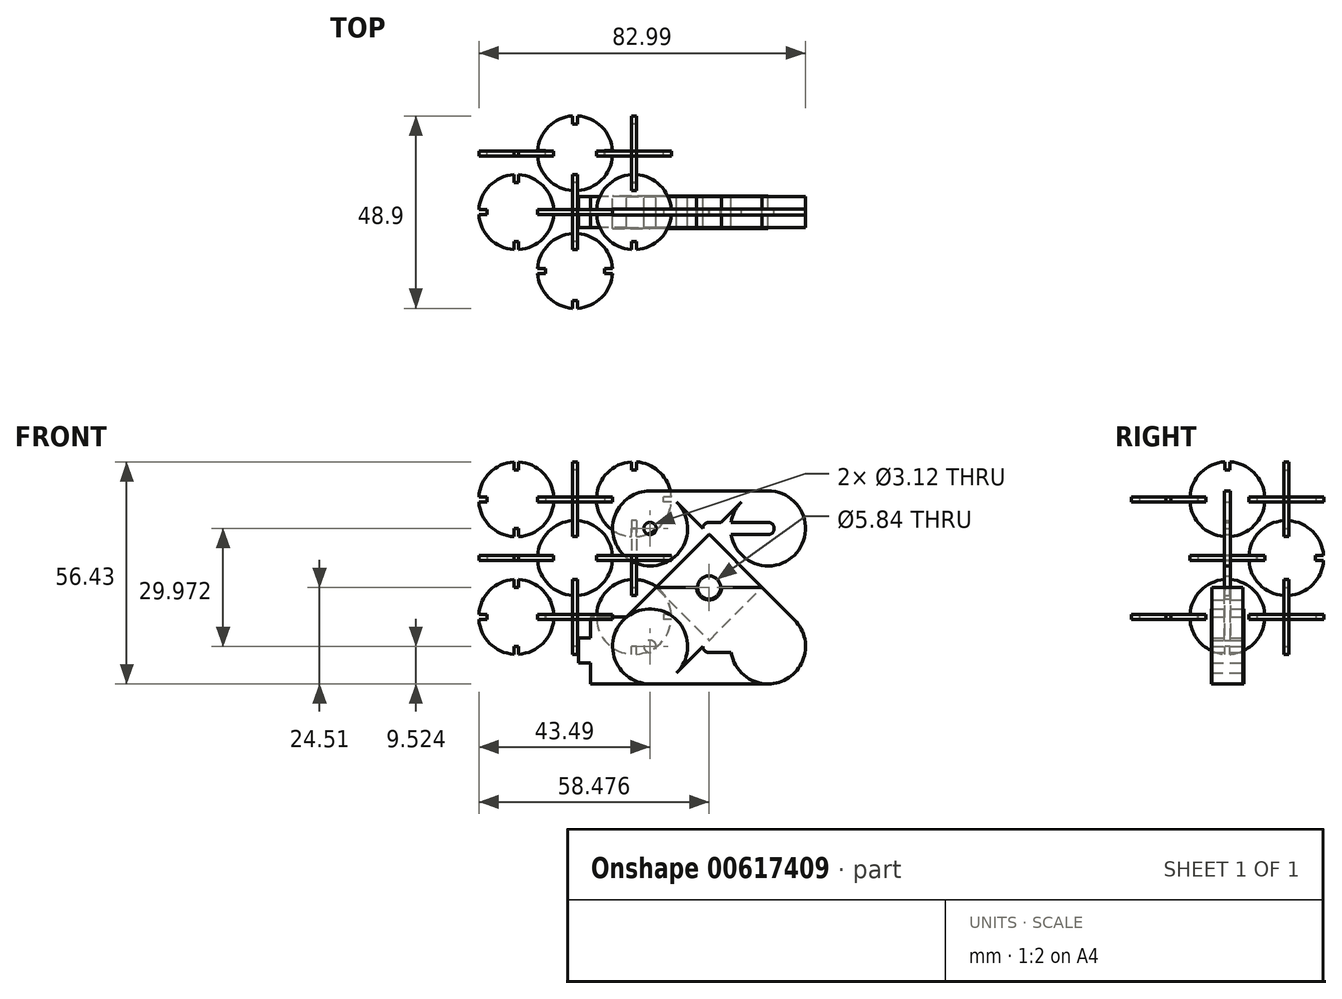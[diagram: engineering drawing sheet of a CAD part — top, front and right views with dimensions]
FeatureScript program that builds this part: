
annotation { "Feature Type Name" : "Feature", "Feature Type Description" : "" }
export const myFeature = defineFeature(function(context is Context, id is Id, definition is map)
    precondition{}
    {
        {
            var Q0;
            Q0=qCreatedBy(makeId("Front.planeOp"),FACE);
            var sketch = newSketch(context, id + "F0", { "sketchPlane" : qUnion([Q0])});
            skArc(sketch, "E0", {"start": v(-0.64, 16.98) * mm, "mid": v(-6.74, 14.2) * mm, "end": v(-9.5, 8.1) * mm});
            skLineSegment(sketch, "E1.top", {"start": v(-0.64, 14.94) * mm, "end": v(0.64, 14.94) * mm});
            skLineSegment(sketch, "E1.left", {"start": v(-0.64, 16.98) * mm, "end": v(-0.64, 14.94) * mm});
            skLineSegment(sketch, "E1.right", {"start": v(0.64, 16.98) * mm, "end": v(0.64, 14.94) * mm});
            skLineSegment(sketch, "E2.1.0", {"start": v(-9.5, 8.1) * mm, "end": v(-7.47, 8.1) * mm});
            skLineSegment(sketch, "E2.1.1", {"start": v(-7.47, 6.84) * mm, "end": v(-7.47, 8.1) * mm});
            skLineSegment(sketch, "E2.1.2", {"start": v(-9.5, 6.84) * mm, "end": v(-7.47, 6.84) * mm});
            skLineSegment(sketch, "E2.2.0", {"start": v(-0.64, -2.03) * mm, "end": v(-0.64, 0) * mm});
            skLineSegment(sketch, "E2.2.1", {"start": v(0.63, 0) * mm, "end": v(-0.64, 0) * mm});
            skLineSegment(sketch, "E2.2.2", {"start": v(0.63, -2.03) * mm, "end": v(0.63, 0) * mm});
            skLineSegment(sketch, "E2.3.0", {"start": v(9.5, 6.84) * mm, "end": v(7.47, 6.84) * mm});
            skLineSegment(sketch, "E2.3.1", {"start": v(7.47, 8.1) * mm, "end": v(7.47, 6.84) * mm});
            skLineSegment(sketch, "E2.3.2", {"start": v(9.5, 8.1) * mm, "end": v(7.47, 8.1) * mm});
            skArc(sketch, "E3.trimOffspring", {"start": v(9.5, 8.1) * mm, "mid": v(6.74, 14.2) * mm, "end": v(0.63, 16.98) * mm});
            skArc(sketch, "E4.trimOffspring", {"start": v(-9.5, 6.84) * mm, "mid": v(-6.74, 0.74) * mm, "end": v(-0.64, -2.03) * mm});
            skArc(sketch, "E5.trimOffspring", {"start": v(0.63, -2.03) * mm, "mid": v(6.74, 0.74) * mm, "end": v(9.5, 6.84) * mm});
            skSolve(sketch);
        }
        {
            var Q0;
            Q0=qCreatedBy(makeId("Right.planeOp"),FACE);
            var sketch = newSketch(context, id + "F1", { "sketchPlane" : qUnion([Q0])});
            skArc(sketch, "E6", {"start": v(-0.64, 2.03) * mm, "mid": v(-6.74, -0.74) * mm, "end": v(-9.5, -6.84) * mm});
            skLineSegment(sketch, "E7.top", {"start": v(-0.64, 0) * mm, "end": v(0.64, 0) * mm});
            skLineSegment(sketch, "E7.left", {"start": v(-0.64, 2.03) * mm, "end": v(-0.64, 0) * mm});
            skLineSegment(sketch, "E7.right", {"start": v(0.64, 2.03) * mm, "end": v(0.64, 0) * mm});
            skLineSegment(sketch, "E8.1.0", {"start": v(-9.5, -6.84) * mm, "end": v(-7.47, -6.84) * mm});
            skLineSegment(sketch, "E8.1.1", {"start": v(-7.47, -8.1) * mm, "end": v(-7.47, -6.84) * mm});
            skLineSegment(sketch, "E8.1.2", {"start": v(-9.5, -8.1) * mm, "end": v(-7.47, -8.1) * mm});
            skLineSegment(sketch, "E8.2.0", {"start": v(-0.64, -16.98) * mm, "end": v(-0.64, -14.94) * mm});
            skLineSegment(sketch, "E8.2.1", {"start": v(0.63, -14.94) * mm, "end": v(-0.64, -14.94) * mm});
            skLineSegment(sketch, "E8.2.2", {"start": v(0.63, -16.98) * mm, "end": v(0.63, -14.94) * mm});
            skLineSegment(sketch, "E8.3.0", {"start": v(9.5, -8.1) * mm, "end": v(7.47, -8.1) * mm});
            skLineSegment(sketch, "E8.3.1", {"start": v(7.47, -6.84) * mm, "end": v(7.47, -8.1) * mm});
            skLineSegment(sketch, "E8.3.2", {"start": v(9.5, -6.84) * mm, "end": v(7.47, -6.84) * mm});
            skArc(sketch, "E9.trimOffspring", {"start": v(9.5, -6.84) * mm, "mid": v(6.74, -0.74) * mm, "end": v(0.64, 2.03) * mm});
            skArc(sketch, "E10.trimOffspring", {"start": v(-9.5, -8.1) * mm, "mid": v(-6.74, -14.2) * mm, "end": v(-0.64, -16.98) * mm});
            skArc(sketch, "E11.trimOffspring", {"start": v(0.63, -16.98) * mm, "mid": v(6.74, -14.2) * mm, "end": v(9.5, -8.1) * mm});
            skArc(sketch, "E12", {"start": v(-0.64, 31.92) * mm, "mid": v(-6.74, 29.15) * mm, "end": v(-9.5, 23.05) * mm});
            skLineSegment(sketch, "E13.top", {"start": v(-0.64, 29.89) * mm, "end": v(0.64, 29.89) * mm});
            skLineSegment(sketch, "E13.left", {"start": v(-0.64, 31.92) * mm, "end": v(-0.64, 29.89) * mm});
            skLineSegment(sketch, "E13.right", {"start": v(0.64, 31.92) * mm, "end": v(0.64, 29.89) * mm});
            skLineSegment(sketch, "E14.1.0", {"start": v(-9.5, 23.05) * mm, "end": v(-7.47, 23.05) * mm});
            skLineSegment(sketch, "E14.1.1", {"start": v(-7.47, 21.78) * mm, "end": v(-7.47, 23.05) * mm});
            skLineSegment(sketch, "E14.1.2", {"start": v(-9.5, 21.78) * mm, "end": v(-7.47, 21.78) * mm});
            skLineSegment(sketch, "E14.2.0", {"start": v(-0.64, 12.91) * mm, "end": v(-0.64, 14.94) * mm});
            skLineSegment(sketch, "E14.2.1", {"start": v(0.63, 14.94) * mm, "end": v(-0.64, 14.94) * mm});
            skLineSegment(sketch, "E14.2.2", {"start": v(0.64, 12.91) * mm, "end": v(0.64, 14.94) * mm});
            skLineSegment(sketch, "E14.3.0", {"start": v(9.5, 21.78) * mm, "end": v(7.47, 21.78) * mm});
            skLineSegment(sketch, "E14.3.1", {"start": v(7.47, 23.05) * mm, "end": v(7.47, 21.78) * mm});
            skLineSegment(sketch, "E14.3.2", {"start": v(9.5, 23.05) * mm, "end": v(7.47, 23.05) * mm});
            skArc(sketch, "E15.trimOffspring", {"start": v(9.5, 23.05) * mm, "mid": v(6.74, 29.15) * mm, "end": v(0.63, 31.92) * mm});
            skArc(sketch, "E16.trimOffspring", {"start": v(-9.5, 21.78) * mm, "mid": v(-6.74, 15.68) * mm, "end": v(-0.64, 12.91) * mm});
            skArc(sketch, "E17.trimOffspring", {"start": v(0.64, 12.91) * mm, "mid": v(6.74, 15.68) * mm, "end": v(9.5, 21.78) * mm});
            skSolve(sketch);
        }
        {
            var Q0;
            Q0=qCreatedBy(makeId("Top.planeOp"),FACE);
            cPlane(context, id + "F2", {"entities" : qUnion([Q0]), "cplaneType" : CPlaneType.OFFSET, "offset" : 7.47 * mm, "width" : 152.4 * mm, "height" : 152.4 * mm});
        }
        {
            var Q0;
            Q0=qCreatedBy(makeId("Top.planeOp"),FACE);
            cPlane(context, id + "F3", {"entities" : qUnion([Q0]), "cplaneType" : CPlaneType.OFFSET, "offset" : 7.47 * mm, "oppositeDirection" : true, "width" : 152.4 * mm, "height" : 152.4 * mm});
        }
        {
            var Q0;
            Q0=qCreatedBy(id+"F2.planeOp",FACE);
            cPlane(context, id + "F4", {"entities" : qUnion([Q0]), "cplaneType" : CPlaneType.OFFSET, "offset" : 7.47 * mm, "width" : 152.4 * mm, "height" : 152.4 * mm});
        }
        {
            var Q0;
            Q0=qCreatedBy(id+"F4.planeOp",FACE);
            cPlane(context, id + "F5", {"entities" : qUnion([Q0]), "cplaneType" : CPlaneType.OFFSET, "offset" : 7.47 * mm, "width" : 152.4 * mm, "height" : 152.4 * mm});
        }
        {
            var Q0;
            Q0=qCreatedBy(makeId("Right.planeOp"),FACE);
            cPlane(context, id + "F6", {"entities" : qUnion([Q0]), "cplaneType" : CPlaneType.OFFSET, "offset" : 7.47 * mm, "width" : 152.4 * mm, "height" : 152.4 * mm});
        }
        {
            var Q0;
            Q0=qCreatedBy(id+"F6.planeOp",FACE);
            cPlane(context, id + "F7", {"entities" : qUnion([Q0]), "cplaneType" : CPlaneType.OFFSET, "offset" : 7.47 * mm, "width" : 152.4 * mm, "height" : 152.4 * mm});
        }
        {
            var Q0;
            Q0=qCreatedBy(makeId("Right.planeOp"),FACE);
            cPlane(context, id + "F8", {"entities" : qUnion([Q0]), "cplaneType" : CPlaneType.OFFSET, "offset" : 7.47 * mm, "oppositeDirection" : true, "width" : 152.4 * mm, "height" : 152.4 * mm});
        }
        {
            var Q0;
            Q0=qCreatedBy(id+"F8.planeOp",FACE);
            cPlane(context, id + "F9", {"entities" : qUnion([Q0]), "cplaneType" : CPlaneType.OFFSET, "offset" : 7.47 * mm, "oppositeDirection" : true, "width" : 152.4 * mm, "height" : 152.4 * mm});
        }
        {
            var Q0;
            Q0=qCreatedBy(makeId("Front.planeOp"),FACE);
            cPlane(context, id + "F10", {"entities" : qUnion([Q0]), "cplaneType" : CPlaneType.OFFSET, "offset" : 7.47 * mm, "width" : 152.4 * mm, "height" : 152.4 * mm});
        }
        {
            var Q0;
            Q0=qCreatedBy(id+"F10.planeOp",FACE);
            cPlane(context, id + "F11", {"entities" : qUnion([Q0]), "cplaneType" : CPlaneType.OFFSET, "offset" : 7.47 * mm, "width" : 152.4 * mm, "height" : 152.4 * mm});
        }
        {
            var Q0;
            Q0=qCreatedBy(makeId("Front.planeOp"),FACE);
            cPlane(context, id + "F12", {"entities" : qUnion([Q0]), "cplaneType" : CPlaneType.OFFSET, "offset" : 7.47 * mm, "oppositeDirection" : true, "width" : 152.4 * mm, "height" : 152.4 * mm});
        }
        {
            var Q0;
            Q0=qCreatedBy(id+"F12.planeOp",FACE);
            cPlane(context, id + "F13", {"entities" : qUnion([Q0]), "cplaneType" : CPlaneType.OFFSET, "offset" : 7.47 * mm, "oppositeDirection" : true, "width" : 152.4 * mm, "height" : 152.4 * mm});
        }
        {
            var Q0;
            Q0=qCreatedBy(id+"F2.planeOp",FACE);
            var sketch = newSketch(context, id + "F14", { "sketchPlane" : qUnion([Q0])});
            skArc(sketch, "E18", {"start": v(14.3, 9.5) * mm, "mid": v(8.2, 6.74) * mm, "end": v(5.43, 0.63) * mm});
            skLineSegment(sketch, "E19.top", {"start": v(14.3, 7.47) * mm, "end": v(15.57, 7.47) * mm});
            skLineSegment(sketch, "E19.left", {"start": v(14.3, 9.5) * mm, "end": v(14.3, 7.47) * mm});
            skLineSegment(sketch, "E19.right", {"start": v(15.57, 9.5) * mm, "end": v(15.57, 7.47) * mm});
            skLineSegment(sketch, "E20.1.0", {"start": v(5.43, 0.64) * mm, "end": v(7.46, 0.64) * mm});
            skLineSegment(sketch, "E20.1.1", {"start": v(7.46, -0.64) * mm, "end": v(7.46, 0.64) * mm});
            skLineSegment(sketch, "E20.1.2", {"start": v(5.43, -0.64) * mm, "end": v(7.46, -0.64) * mm});
            skLineSegment(sketch, "E20.2.0", {"start": v(14.3, -9.5) * mm, "end": v(14.3, -7.47) * mm});
            skLineSegment(sketch, "E20.2.1", {"start": v(15.57, -7.47) * mm, "end": v(14.3, -7.47) * mm});
            skLineSegment(sketch, "E20.2.2", {"start": v(15.57, -9.5) * mm, "end": v(15.57, -7.47) * mm});
            skLineSegment(sketch, "E20.3.0", {"start": v(24.44, -0.64) * mm, "end": v(22.4, -0.64) * mm});
            skLineSegment(sketch, "E20.3.1", {"start": v(22.4, 0.64) * mm, "end": v(22.4, -0.64) * mm});
            skLineSegment(sketch, "E20.3.2", {"start": v(24.44, 0.64) * mm, "end": v(22.4, 0.64) * mm});
            skArc(sketch, "E21.trimOffspring", {"start": v(24.44, 0.64) * mm, "mid": v(21.67, 6.74) * mm, "end": v(15.57, 9.5) * mm});
            skArc(sketch, "E22.trimOffspring", {"start": v(5.43, -0.63) * mm, "mid": v(8.2, -6.74) * mm, "end": v(14.3, -9.5) * mm});
            skArc(sketch, "E23.trimOffspring", {"start": v(15.57, -9.5) * mm, "mid": v(21.67, -6.74) * mm, "end": v(24.44, -0.63) * mm});
            skArc(sketch, "E24", {"start": v(-15.57, 9.5) * mm, "mid": v(-21.67, 6.74) * mm, "end": v(-24.44, 0.63) * mm});
            skLineSegment(sketch, "E25.top", {"start": v(-15.57, 7.47) * mm, "end": v(-14.3, 7.47) * mm});
            skLineSegment(sketch, "E25.left", {"start": v(-15.57, 9.5) * mm, "end": v(-15.57, 7.47) * mm});
            skLineSegment(sketch, "E25.right", {"start": v(-14.3, 9.5) * mm, "end": v(-14.3, 7.47) * mm});
            skLineSegment(sketch, "E26.1.0", {"start": v(-24.44, 0.63) * mm, "end": v(-22.4, 0.63) * mm});
            skLineSegment(sketch, "E26.1.1", {"start": v(-22.4, -0.64) * mm, "end": v(-22.4, 0.64) * mm});
            skLineSegment(sketch, "E26.1.2", {"start": v(-24.44, -0.64) * mm, "end": v(-22.4, -0.64) * mm});
            skLineSegment(sketch, "E26.2.0", {"start": v(-15.57, -9.5) * mm, "end": v(-15.57, -7.47) * mm});
            skLineSegment(sketch, "E26.2.1", {"start": v(-14.3, -7.47) * mm, "end": v(-15.57, -7.47) * mm});
            skLineSegment(sketch, "E26.2.2", {"start": v(-14.3, -9.5) * mm, "end": v(-14.3, -7.47) * mm});
            skLineSegment(sketch, "E26.3.0", {"start": v(-5.43, -0.64) * mm, "end": v(-7.46, -0.64) * mm});
            skLineSegment(sketch, "E26.3.1", {"start": v(-7.46, 0.64) * mm, "end": v(-7.46, -0.64) * mm});
            skLineSegment(sketch, "E26.3.2", {"start": v(-5.43, 0.64) * mm, "end": v(-7.46, 0.64) * mm});
            skArc(sketch, "E27.trimOffspring", {"start": v(-5.43, 0.63) * mm, "mid": v(-8.2, 6.74) * mm, "end": v(-14.3, 9.5) * mm});
            skArc(sketch, "E28.trimOffspring", {"start": v(-24.44, -0.63) * mm, "mid": v(-21.67, -6.74) * mm, "end": v(-15.57, -9.5) * mm});
            skArc(sketch, "E29.trimOffspring", {"start": v(-14.3, -9.5) * mm, "mid": v(-8.2, -6.74) * mm, "end": v(-5.43, -0.63) * mm});
            skSolve(sketch);
        }
        {
            var Q0;
            Q0=qCreatedBy(id+"F13.planeOp",FACE);
            var sketch = newSketch(context, id + "F15", { "sketchPlane" : qUnion([Q0])});
            skArc(sketch, "E30", {"start": v(-15.57, 31.91) * mm, "mid": v(-21.67, 29.14) * mm, "end": v(-24.44, 23.04) * mm});
            skLineSegment(sketch, "E31.top", {"start": v(-15.57, 29.88) * mm, "end": v(-14.3, 29.88) * mm});
            skLineSegment(sketch, "E31.left", {"start": v(-15.57, 31.91) * mm, "end": v(-15.57, 29.88) * mm});
            skLineSegment(sketch, "E31.right", {"start": v(-14.3, 31.91) * mm, "end": v(-14.3, 29.88) * mm});
            skLineSegment(sketch, "E32.1.0", {"start": v(-24.44, 23.04) * mm, "end": v(-22.4, 23.04) * mm});
            skLineSegment(sketch, "E32.1.1", {"start": v(-22.4, 21.77) * mm, "end": v(-22.4, 23.04) * mm});
            skLineSegment(sketch, "E32.1.2", {"start": v(-24.44, 21.77) * mm, "end": v(-22.4, 21.77) * mm});
            skLineSegment(sketch, "E32.2.0", {"start": v(-15.57, 12.9) * mm, "end": v(-15.57, 14.94) * mm});
            skLineSegment(sketch, "E32.2.1", {"start": v(-14.3, 14.94) * mm, "end": v(-15.57, 14.94) * mm});
            skLineSegment(sketch, "E32.2.2", {"start": v(-14.3, 12.9) * mm, "end": v(-14.3, 14.94) * mm});
            skLineSegment(sketch, "E32.3.0", {"start": v(-5.43, 21.77) * mm, "end": v(-7.46, 21.77) * mm});
            skLineSegment(sketch, "E32.3.1", {"start": v(-7.46, 23.04) * mm, "end": v(-7.46, 21.77) * mm});
            skLineSegment(sketch, "E32.3.2", {"start": v(-5.43, 23.04) * mm, "end": v(-7.46, 23.04) * mm});
            skArc(sketch, "E33.trimOffspring", {"start": v(-5.43, 23.04) * mm, "mid": v(-8.2, 29.14) * mm, "end": v(-14.3, 31.91) * mm});
            skArc(sketch, "E34.trimOffspring", {"start": v(-24.44, 21.77) * mm, "mid": v(-21.67, 15.67) * mm, "end": v(-15.57, 12.9) * mm});
            skArc(sketch, "E35.trimOffspring", {"start": v(-14.3, 12.9) * mm, "mid": v(-8.2, 15.67) * mm, "end": v(-5.43, 21.77) * mm});
            skLineSegment(sketch, "E36.MirrorCS", {"start": v(-15.57, -16.98) * mm, "end": v(-15.57, -14.94) * mm});
            skLineSegment(sketch, "E37.MirrorCS", {"start": v(-14.3, -16.98) * mm, "end": v(-14.3, -14.94) * mm});
            skLineSegment(sketch, "E38.MirrorCS", {"start": v(-15.57, 2.03) * mm, "end": v(-15.57, 0) * mm});
            skLineSegment(sketch, "E39.MirrorCS", {"start": v(-24.44, -6.84) * mm, "end": v(-22.4, -6.84) * mm});
            skLineSegment(sketch, "E40.MirrorCS", {"start": v(-5.43, -8.1) * mm, "end": v(-7.46, -8.1) * mm});
            skLineSegment(sketch, "E41.MirrorCS", {"start": v(-24.44, -8.1) * mm, "end": v(-22.4, -8.1) * mm});
            skLineSegment(sketch, "E42.MirrorCS", {"start": v(-22.4, -6.84) * mm, "end": v(-22.4, -8.1) * mm});
            skLineSegment(sketch, "E43.MirrorCS", {"start": v(-14.3, 0) * mm, "end": v(-15.57, 0) * mm});
            skLineSegment(sketch, "E44.MirrorCS", {"start": v(-5.43, -6.84) * mm, "end": v(-7.46, -6.84) * mm});
            skLineSegment(sketch, "E45.MirrorCS", {"start": v(-15.57, -14.94) * mm, "end": v(-14.3, -14.94) * mm});
            skLineSegment(sketch, "E46.MirrorCS", {"start": v(-14.3, 2.03) * mm, "end": v(-14.3, 0) * mm});
            skLineSegment(sketch, "E47.MirrorCS", {"start": v(-7.46, -8.1) * mm, "end": v(-7.46, -6.84) * mm});
            skArc(sketch, "E48.MirrorCS", {"start": v(-5.43, -8.1) * mm, "mid": v(-8.2, -14.2) * mm, "end": v(-14.3, -16.98) * mm});
            skArc(sketch, "E49.MirrorCS", {"start": v(-14.3, 2.03) * mm, "mid": v(-8.2, -0.74) * mm, "end": v(-5.43, -6.84) * mm});
            skArc(sketch, "E50.MirrorCS", {"start": v(-24.44, -6.84) * mm, "mid": v(-21.67, -0.74) * mm, "end": v(-15.57, 2.03) * mm});
            skArc(sketch, "E51.MirrorCS", {"start": v(-15.57, -16.98) * mm, "mid": v(-21.67, -14.2) * mm, "end": v(-24.44, -8.1) * mm});
            skLineSegment(sketch, "E52.MirrorCS", {"start": v(7.46, -8.1) * mm, "end": v(7.46, -6.84) * mm});
            skLineSegment(sketch, "E53.MirrorCS", {"start": v(15.57, -16.98) * mm, "end": v(15.57, -14.94) * mm});
            skLineSegment(sketch, "E54.MirrorCS", {"start": v(5.43, 23.04) * mm, "end": v(7.46, 23.04) * mm});
            skLineSegment(sketch, "E55.MirrorCS", {"start": v(24.44, -8.1) * mm, "end": v(22.4, -8.1) * mm});
            skLineSegment(sketch, "E56.MirrorCS", {"start": v(24.44, 23.04) * mm, "end": v(22.4, 23.04) * mm});
            skLineSegment(sketch, "E57.MirrorCS", {"start": v(22.4, 21.77) * mm, "end": v(22.4, 23.04) * mm});
            skLineSegment(sketch, "E58.MirrorCS", {"start": v(24.44, -6.84) * mm, "end": v(22.4, -6.84) * mm});
            skLineSegment(sketch, "E59.MirrorCS", {"start": v(14.3, 12.9) * mm, "end": v(14.3, 14.94) * mm});
            skLineSegment(sketch, "E60.MirrorCS", {"start": v(15.57, 31.91) * mm, "end": v(15.57, 29.88) * mm});
            skLineSegment(sketch, "E61.MirrorCS", {"start": v(5.43, -6.84) * mm, "end": v(7.46, -6.84) * mm});
            skLineSegment(sketch, "E62.MirrorCS", {"start": v(5.43, 21.77) * mm, "end": v(7.46, 21.77) * mm});
            skLineSegment(sketch, "E63.MirrorCS", {"start": v(7.46, 23.04) * mm, "end": v(7.46, 21.77) * mm});
            skLineSegment(sketch, "E64.MirrorCS", {"start": v(14.3, 2.03) * mm, "end": v(14.3, 0) * mm});
            skLineSegment(sketch, "E65.MirrorCS", {"start": v(15.57, 2.03) * mm, "end": v(15.57, 0) * mm});
            skLineSegment(sketch, "E66.MirrorCS", {"start": v(5.43, -8.1) * mm, "end": v(7.46, -8.1) * mm});
            skLineSegment(sketch, "E67.MirrorCS", {"start": v(14.3, -16.98) * mm, "end": v(14.3, -14.94) * mm});
            skLineSegment(sketch, "E68.MirrorCS", {"start": v(24.44, 21.77) * mm, "end": v(22.4, 21.77) * mm});
            skLineSegment(sketch, "E69.MirrorCS", {"start": v(15.57, -14.94) * mm, "end": v(14.3, -14.94) * mm});
            skLineSegment(sketch, "E70.MirrorCS", {"start": v(22.4, -6.84) * mm, "end": v(22.4, -8.1) * mm});
            skLineSegment(sketch, "E71.MirrorCS", {"start": v(14.3, 0) * mm, "end": v(15.57, 0) * mm});
            skLineSegment(sketch, "E72.MirrorCS", {"start": v(14.3, 31.91) * mm, "end": v(14.3, 29.88) * mm});
            skLineSegment(sketch, "E73.MirrorCS", {"start": v(14.3, 14.94) * mm, "end": v(15.57, 14.94) * mm});
            skLineSegment(sketch, "E74.MirrorCS", {"start": v(15.57, 29.88) * mm, "end": v(14.3, 29.88) * mm});
            skLineSegment(sketch, "E75.MirrorCS", {"start": v(15.57, 12.9) * mm, "end": v(15.57, 14.94) * mm});
            skArc(sketch, "E76.MirrorCS", {"start": v(14.3, 12.9) * mm, "mid": v(8.2, 15.67) * mm, "end": v(5.43, 21.77) * mm});
            skArc(sketch, "E77.MirrorCS", {"start": v(14.3, 2.03) * mm, "mid": v(8.2, -0.74) * mm, "end": v(5.43, -6.84) * mm});
            skArc(sketch, "E78.MirrorCS", {"start": v(5.43, -8.1) * mm, "mid": v(8.2, -14.2) * mm, "end": v(14.3, -16.98) * mm});
            skArc(sketch, "E79.MirrorCS", {"start": v(24.44, 21.77) * mm, "mid": v(21.67, 15.67) * mm, "end": v(15.57, 12.9) * mm});
            skArc(sketch, "E80.MirrorCS", {"start": v(15.57, -16.98) * mm, "mid": v(21.67, -14.2) * mm, "end": v(24.44, -8.1) * mm});
            skArc(sketch, "E81.MirrorCS", {"start": v(5.43, 23.04) * mm, "mid": v(8.2, 29.14) * mm, "end": v(14.3, 31.91) * mm});
            skArc(sketch, "E82.MirrorCS", {"start": v(24.44, -6.84) * mm, "mid": v(21.67, -0.74) * mm, "end": v(15.57, 2.03) * mm});
            skArc(sketch, "E83.MirrorCS", {"start": v(15.57, 31.91) * mm, "mid": v(21.67, 29.14) * mm, "end": v(24.44, 23.04) * mm});
            skSolve(sketch);
        }
        {
            var Q0;
            Q0=qCreatedBy(id+"F11.planeOp",FACE);
            var sketch = newSketch(context, id + "F16", { "sketchPlane" : qUnion([Q0])});
            skArc(sketch, "E84", {"start": v(14.3, 2.03) * mm, "mid": v(8.2, -0.73) * mm, "end": v(5.43, -6.83) * mm});
            skLineSegment(sketch, "E85.top", {"start": v(14.3, 0) * mm, "end": v(15.57, 0) * mm});
            skLineSegment(sketch, "E85.left", {"start": v(14.3, 2.03) * mm, "end": v(14.3, 0) * mm});
            skLineSegment(sketch, "E85.right", {"start": v(15.57, 2.03) * mm, "end": v(15.57, 0) * mm});
            skLineSegment(sketch, "E86.1.0", {"start": v(5.43, -6.83) * mm, "end": v(7.46, -6.83) * mm});
            skLineSegment(sketch, "E86.1.1", {"start": v(7.46, -8.1) * mm, "end": v(7.46, -6.83) * mm});
            skLineSegment(sketch, "E86.1.2", {"start": v(5.43, -8.1) * mm, "end": v(7.46, -8.1) * mm});
            skLineSegment(sketch, "E86.2.0", {"start": v(14.3, -16.98) * mm, "end": v(14.3, -14.94) * mm});
            skLineSegment(sketch, "E86.2.1", {"start": v(15.57, -14.94) * mm, "end": v(14.3, -14.94) * mm});
            skLineSegment(sketch, "E86.2.2", {"start": v(15.57, -16.98) * mm, "end": v(15.57, -14.94) * mm});
            skLineSegment(sketch, "E86.3.0", {"start": v(24.44, -8.11) * mm, "end": v(22.4, -8.11) * mm});
            skLineSegment(sketch, "E86.3.1", {"start": v(22.4, -6.84) * mm, "end": v(22.4, -8.11) * mm});
            skLineSegment(sketch, "E86.3.2", {"start": v(24.44, -6.84) * mm, "end": v(22.4, -6.84) * mm});
            skArc(sketch, "E87.trimOffspring", {"start": v(24.44, -6.84) * mm, "mid": v(21.67, -0.74) * mm, "end": v(15.57, 2.03) * mm});
            skArc(sketch, "E88.trimOffspring", {"start": v(5.43, -8.1) * mm, "mid": v(8.2, -14.2) * mm, "end": v(14.3, -16.98) * mm});
            skArc(sketch, "E89.trimOffspring", {"start": v(15.57, -16.98) * mm, "mid": v(21.67, -14.21) * mm, "end": v(24.44, -8.11) * mm});
            skLineSegment(sketch, "E90.MirrorCS", {"start": v(22.4, 21.78) * mm, "end": v(22.4, 23.05) * mm});
            skLineSegment(sketch, "E91.MirrorCS", {"start": v(15.57, 29.88) * mm, "end": v(14.3, 29.88) * mm});
            skLineSegment(sketch, "E92.MirrorCS", {"start": v(7.46, 23.04) * mm, "end": v(7.46, 21.77) * mm});
            skLineSegment(sketch, "E93.MirrorCS", {"start": v(14.3, 14.93) * mm, "end": v(15.57, 14.93) * mm});
            skLineSegment(sketch, "E94.MirrorCS", {"start": v(24.44, 21.78) * mm, "end": v(22.4, 21.78) * mm});
            skLineSegment(sketch, "E95.MirrorCS", {"start": v(15.57, 31.91) * mm, "end": v(15.57, 29.88) * mm});
            skLineSegment(sketch, "E96.MirrorCS", {"start": v(24.44, 23.05) * mm, "end": v(22.4, 23.05) * mm});
            skLineSegment(sketch, "E97.MirrorCS", {"start": v(14.3, 31.91) * mm, "end": v(14.3, 29.88) * mm});
            skArc(sketch, "E98.MirrorCS", {"start": v(5.43, 23.04) * mm, "mid": v(8.2, 29.14) * mm, "end": v(14.3, 31.91) * mm});
            skArc(sketch, "E99.MirrorCS", {"start": v(14.3, 12.9) * mm, "mid": v(8.2, 15.67) * mm, "end": v(5.43, 21.77) * mm});
            skLineSegment(sketch, "E100.MirrorCS", {"start": v(5.43, 21.77) * mm, "end": v(7.46, 21.77) * mm});
            skLineSegment(sketch, "E101.MirrorCS", {"start": v(15.57, 12.9) * mm, "end": v(15.57, 14.93) * mm});
            skArc(sketch, "E102.MirrorCS", {"start": v(15.57, 31.91) * mm, "mid": v(21.67, 29.15) * mm, "end": v(24.44, 23.05) * mm});
            skLineSegment(sketch, "E103.MirrorCS", {"start": v(5.43, 23.04) * mm, "end": v(7.46, 23.04) * mm});
            skLineSegment(sketch, "E104.MirrorCS", {"start": v(14.3, 12.9) * mm, "end": v(14.3, 14.93) * mm});
            skArc(sketch, "E105.MirrorCS", {"start": v(24.44, 21.78) * mm, "mid": v(21.67, 15.68) * mm, "end": v(15.57, 12.9) * mm});
            skLineSegment(sketch, "E106.MirrorCS", {"start": v(-7.46, -8.1) * mm, "end": v(-7.46, -6.83) * mm});
            skLineSegment(sketch, "E107.MirrorCS", {"start": v(-14.3, 14.93) * mm, "end": v(-15.57, 14.93) * mm});
            skLineSegment(sketch, "E108.MirrorCS", {"start": v(-15.57, 29.88) * mm, "end": v(-14.3, 29.88) * mm});
            skLineSegment(sketch, "E109.MirrorCS", {"start": v(-14.3, 0) * mm, "end": v(-15.57, 0) * mm});
            skLineSegment(sketch, "E110.MirrorCS", {"start": v(-7.46, 23.04) * mm, "end": v(-7.46, 21.77) * mm});
            skLineSegment(sketch, "E111.MirrorCS", {"start": v(-22.4, 21.78) * mm, "end": v(-22.4, 23.05) * mm});
            skLineSegment(sketch, "E112.MirrorCS", {"start": v(-15.57, -14.94) * mm, "end": v(-14.3, -14.94) * mm});
            skLineSegment(sketch, "E113.MirrorCS", {"start": v(-22.4, -6.84) * mm, "end": v(-22.4, -8.11) * mm});
            skLineSegment(sketch, "E114.MirrorCS", {"start": v(-15.57, 31.91) * mm, "end": v(-15.57, 29.88) * mm});
            skLineSegment(sketch, "E115.MirrorCS", {"start": v(-14.3, 31.91) * mm, "end": v(-14.3, 29.88) * mm});
            skLineSegment(sketch, "E116.MirrorCS", {"start": v(-15.57, 12.9) * mm, "end": v(-15.57, 14.93) * mm});
            skLineSegment(sketch, "E117.MirrorCS", {"start": v(-14.3, 12.9) * mm, "end": v(-14.3, 14.93) * mm});
            skLineSegment(sketch, "E118.MirrorCS", {"start": v(-15.57, 2.03) * mm, "end": v(-15.57, 0) * mm});
            skLineSegment(sketch, "E119.MirrorCS", {"start": v(-5.43, -6.83) * mm, "end": v(-7.46, -6.83) * mm});
            skLineSegment(sketch, "E120.MirrorCS", {"start": v(-5.43, -8.1) * mm, "end": v(-7.46, -8.1) * mm});
            skLineSegment(sketch, "E121.MirrorCS", {"start": v(-14.3, -16.98) * mm, "end": v(-14.3, -14.94) * mm});
            skArc(sketch, "E122.MirrorCS", {"start": v(-24.44, -6.84) * mm, "mid": v(-21.67, -0.74) * mm, "end": v(-15.57, 2.03) * mm});
            skLineSegment(sketch, "E123.MirrorCS", {"start": v(-5.43, 23.04) * mm, "end": v(-7.46, 23.04) * mm});
            skLineSegment(sketch, "E124.MirrorCS", {"start": v(-14.3, 2.03) * mm, "end": v(-14.3, 0) * mm});
            skArc(sketch, "E125.MirrorCS", {"start": v(-15.57, 31.91) * mm, "mid": v(-21.67, 29.15) * mm, "end": v(-24.44, 23.05) * mm});
            skLineSegment(sketch, "E126.MirrorCS", {"start": v(-24.44, 21.78) * mm, "end": v(-22.4, 21.78) * mm});
            skArc(sketch, "E127.MirrorCS", {"start": v(-14.3, 2.03) * mm, "mid": v(-8.2, -0.73) * mm, "end": v(-5.43, -6.83) * mm});
            skLineSegment(sketch, "E128.MirrorCS", {"start": v(-24.44, -8.11) * mm, "end": v(-22.4, -8.11) * mm});
            skArc(sketch, "E129.MirrorCS", {"start": v(-24.44, 21.78) * mm, "mid": v(-21.67, 15.68) * mm, "end": v(-15.57, 12.9) * mm});
            skArc(sketch, "E130.MirrorCS", {"start": v(-5.43, 23.04) * mm, "mid": v(-8.2, 29.14) * mm, "end": v(-14.3, 31.91) * mm});
            skArc(sketch, "E131.MirrorCS", {"start": v(-5.43, -8.1) * mm, "mid": v(-8.2, -14.2) * mm, "end": v(-14.3, -16.98) * mm});
            skLineSegment(sketch, "E132.MirrorCS", {"start": v(-5.43, 21.77) * mm, "end": v(-7.46, 21.77) * mm});
            skLineSegment(sketch, "E133.MirrorCS", {"start": v(-24.44, -6.84) * mm, "end": v(-22.4, -6.84) * mm});
            skArc(sketch, "E134.MirrorCS", {"start": v(-14.3, 12.9) * mm, "mid": v(-8.2, 15.67) * mm, "end": v(-5.43, 21.77) * mm});
            skArc(sketch, "E135.MirrorCS", {"start": v(-15.57, -16.98) * mm, "mid": v(-21.67, -14.21) * mm, "end": v(-24.44, -8.11) * mm});
            skLineSegment(sketch, "E136.MirrorCS", {"start": v(-24.44, 23.05) * mm, "end": v(-22.4, 23.05) * mm});
            skLineSegment(sketch, "E137.MirrorCS", {"start": v(-15.57, -16.98) * mm, "end": v(-15.57, -14.94) * mm});
            skSolve(sketch);
        }
        {
            var Q0;
            Q0=qCreatedBy(id+"F3.planeOp",FACE);
            var sketch = newSketch(context, id + "F17", { "sketchPlane" : qUnion([Q0])});
            skArc(sketch, "E138", {"start": v(-0.63, -5.44) * mm, "mid": v(-6.74, -8.2) * mm, "end": v(-9.5, -14.3) * mm});
            skLineSegment(sketch, "E139.top", {"start": v(-0.63, -7.47) * mm, "end": v(0.63, -7.47) * mm});
            skLineSegment(sketch, "E139.left", {"start": v(-0.63, -5.44) * mm, "end": v(-0.63, -7.47) * mm});
            skLineSegment(sketch, "E139.right", {"start": v(0.64, -5.44) * mm, "end": v(0.64, -7.47) * mm});
            skLineSegment(sketch, "E140.1.0", {"start": v(-9.5, -14.3) * mm, "end": v(-7.47, -14.3) * mm});
            skLineSegment(sketch, "E140.1.1", {"start": v(-7.47, -15.58) * mm, "end": v(-7.47, -14.3) * mm});
            skLineSegment(sketch, "E140.1.2", {"start": v(-9.5, -15.58) * mm, "end": v(-7.47, -15.58) * mm});
            skLineSegment(sketch, "E140.2.0", {"start": v(-0.64, -24.45) * mm, "end": v(-0.64, -22.42) * mm});
            skLineSegment(sketch, "E140.2.1", {"start": v(0.63, -22.42) * mm, "end": v(-0.64, -22.42) * mm});
            skLineSegment(sketch, "E140.2.2", {"start": v(0.63, -24.45) * mm, "end": v(0.63, -22.42) * mm});
            skLineSegment(sketch, "E140.3.0", {"start": v(9.5, -15.58) * mm, "end": v(7.47, -15.58) * mm});
            skLineSegment(sketch, "E140.3.1", {"start": v(7.47, -14.3) * mm, "end": v(7.47, -15.58) * mm});
            skLineSegment(sketch, "E140.3.2", {"start": v(9.5, -14.3) * mm, "end": v(7.47, -14.3) * mm});
            skArc(sketch, "E141.trimOffspring", {"start": v(9.5, -14.3) * mm, "mid": v(6.74, -8.2) * mm, "end": v(0.64, -5.44) * mm});
            skArc(sketch, "E142.trimOffspring", {"start": v(-9.5, -15.58) * mm, "mid": v(-6.74, -21.68) * mm, "end": v(-0.64, -24.45) * mm});
            skArc(sketch, "E143.trimOffspring", {"start": v(0.63, -24.45) * mm, "mid": v(6.74, -21.68) * mm, "end": v(9.5, -15.58) * mm});
            skArc(sketch, "E144", {"start": v(-0.63, 24.45) * mm, "mid": v(-6.74, 21.68) * mm, "end": v(-9.5, 15.58) * mm});
            skLineSegment(sketch, "E145.top", {"start": v(-0.63, 22.42) * mm, "end": v(0.64, 22.42) * mm});
            skLineSegment(sketch, "E145.left", {"start": v(-0.63, 24.45) * mm, "end": v(-0.63, 22.42) * mm});
            skLineSegment(sketch, "E145.right", {"start": v(0.64, 24.45) * mm, "end": v(0.64, 22.42) * mm});
            skLineSegment(sketch, "E146.1.0", {"start": v(-9.5, 15.58) * mm, "end": v(-7.47, 15.58) * mm});
            skLineSegment(sketch, "E146.1.1", {"start": v(-7.47, 14.3) * mm, "end": v(-7.47, 15.58) * mm});
            skLineSegment(sketch, "E146.1.2", {"start": v(-9.5, 14.3) * mm, "end": v(-7.47, 14.3) * mm});
            skLineSegment(sketch, "E146.2.0", {"start": v(-0.63, 5.44) * mm, "end": v(-0.64, 7.47) * mm});
            skLineSegment(sketch, "E146.2.1", {"start": v(0.63, 7.47) * mm, "end": v(-0.63, 7.47) * mm});
            skLineSegment(sketch, "E146.2.2", {"start": v(0.63, 5.44) * mm, "end": v(0.64, 7.47) * mm});
            skLineSegment(sketch, "E146.3.0", {"start": v(9.5, 14.3) * mm, "end": v(7.47, 14.3) * mm});
            skLineSegment(sketch, "E146.3.1", {"start": v(7.47, 15.58) * mm, "end": v(7.47, 14.3) * mm});
            skLineSegment(sketch, "E146.3.2", {"start": v(9.5, 15.58) * mm, "end": v(7.47, 15.58) * mm});
            skArc(sketch, "E147.trimOffspring", {"start": v(9.5, 15.58) * mm, "mid": v(6.74, 21.68) * mm, "end": v(0.64, 24.45) * mm});
            skArc(sketch, "E148.trimOffspring", {"start": v(-9.5, 14.3) * mm, "mid": v(-6.74, 8.2) * mm, "end": v(-0.64, 5.44) * mm});
            skArc(sketch, "E149.trimOffspring", {"start": v(0.63, 5.44) * mm, "mid": v(6.74, 8.2) * mm, "end": v(9.5, 14.3) * mm});
            skSolve(sketch);
        }
        {
            var Q0;
            Q0=qCreatedBy(id+"F5.planeOp",FACE);
            var sketch = newSketch(context, id + "F18", { "sketchPlane" : qUnion([Q0])});
            skArc(sketch, "E150", {"start": v(-0.63, -5.44) * mm, "mid": v(-6.74, -8.2) * mm, "end": v(-9.5, -14.3) * mm});
            skLineSegment(sketch, "E151.top", {"start": v(-0.63, -7.47) * mm, "end": v(0.64, -7.47) * mm});
            skLineSegment(sketch, "E151.left", {"start": v(-0.63, -5.44) * mm, "end": v(-0.63, -7.47) * mm});
            skLineSegment(sketch, "E151.right", {"start": v(0.64, -5.44) * mm, "end": v(0.64, -7.47) * mm});
            skLineSegment(sketch, "E152.1.0", {"start": v(-9.5, -14.3) * mm, "end": v(-7.47, -14.3) * mm});
            skLineSegment(sketch, "E152.1.1", {"start": v(-7.47, -15.58) * mm, "end": v(-7.47, -14.3) * mm});
            skLineSegment(sketch, "E152.1.2", {"start": v(-9.5, -15.58) * mm, "end": v(-7.47, -15.58) * mm});
            skLineSegment(sketch, "E152.2.0", {"start": v(-0.64, -24.45) * mm, "end": v(-0.64, -22.42) * mm});
            skLineSegment(sketch, "E152.2.1", {"start": v(0.63, -22.42) * mm, "end": v(-0.64, -22.42) * mm});
            skLineSegment(sketch, "E152.2.2", {"start": v(0.63, -24.45) * mm, "end": v(0.63, -22.42) * mm});
            skLineSegment(sketch, "E152.3.0", {"start": v(9.5, -15.58) * mm, "end": v(7.47, -15.58) * mm});
            skLineSegment(sketch, "E152.3.1", {"start": v(7.47, -14.3) * mm, "end": v(7.47, -15.58) * mm});
            skLineSegment(sketch, "E152.3.2", {"start": v(9.5, -14.3) * mm, "end": v(7.47, -14.3) * mm});
            skArc(sketch, "E153.trimOffspring", {"start": v(9.5, -14.3) * mm, "mid": v(6.74, -8.2) * mm, "end": v(0.64, -5.44) * mm});
            skArc(sketch, "E154.trimOffspring", {"start": v(-9.5, -15.58) * mm, "mid": v(-6.74, -21.68) * mm, "end": v(-0.64, -24.45) * mm});
            skArc(sketch, "E155.trimOffspring", {"start": v(0.63, -24.45) * mm, "mid": v(6.74, -21.68) * mm, "end": v(9.5, -15.58) * mm});
            skArc(sketch, "E156", {"start": v(-0.63, 24.45) * mm, "mid": v(-6.74, 21.68) * mm, "end": v(-9.5, 15.58) * mm});
            skLineSegment(sketch, "E157.top", {"start": v(-0.63, 22.42) * mm, "end": v(0.64, 22.42) * mm});
            skLineSegment(sketch, "E157.left", {"start": v(-0.63, 24.45) * mm, "end": v(-0.63, 22.42) * mm});
            skLineSegment(sketch, "E157.right", {"start": v(0.64, 24.45) * mm, "end": v(0.64, 22.42) * mm});
            skLineSegment(sketch, "E158.1.0", {"start": v(-9.5, 15.58) * mm, "end": v(-7.47, 15.58) * mm});
            skLineSegment(sketch, "E158.1.1", {"start": v(-7.47, 14.3) * mm, "end": v(-7.47, 15.58) * mm});
            skLineSegment(sketch, "E158.1.2", {"start": v(-9.5, 14.3) * mm, "end": v(-7.47, 14.3) * mm});
            skLineSegment(sketch, "E158.2.0", {"start": v(-0.63, 5.44) * mm, "end": v(-0.63, 7.47) * mm});
            skLineSegment(sketch, "E158.2.1", {"start": v(0.64, 7.47) * mm, "end": v(-0.63, 7.47) * mm});
            skLineSegment(sketch, "E158.2.2", {"start": v(0.64, 5.44) * mm, "end": v(0.64, 7.47) * mm});
            skLineSegment(sketch, "E158.3.0", {"start": v(9.5, 14.3) * mm, "end": v(7.47, 14.3) * mm});
            skLineSegment(sketch, "E158.3.1", {"start": v(7.47, 15.58) * mm, "end": v(7.47, 14.3) * mm});
            skLineSegment(sketch, "E158.3.2", {"start": v(9.5, 15.58) * mm, "end": v(7.47, 15.58) * mm});
            skArc(sketch, "E159.trimOffspring", {"start": v(9.5, 15.58) * mm, "mid": v(6.74, 21.68) * mm, "end": v(0.64, 24.45) * mm});
            skArc(sketch, "E160.trimOffspring", {"start": v(-9.5, 14.3) * mm, "mid": v(-6.74, 8.2) * mm, "end": v(-0.63, 5.44) * mm});
            skArc(sketch, "E161.trimOffspring", {"start": v(0.64, 5.44) * mm, "mid": v(6.74, 8.2) * mm, "end": v(9.5, 14.3) * mm});
            skSolve(sketch);
        }
        {
            var Q0;
            Q0=qCreatedBy(id+"F7.planeOp",FACE);
            var sketch = newSketch(context, id + "F19", { "sketchPlane" : qUnion([Q0])});
            skArc(sketch, "E162", {"start": v(5.43, 6.84) * mm, "mid": v(8.2, 0.74) * mm, "end": v(14.3, -2.03) * mm});
            skLineSegment(sketch, "E163.top", {"start": v(7.46, 6.84) * mm, "end": v(7.46, 8.1) * mm});
            skLineSegment(sketch, "E163.left", {"start": v(5.43, 6.84) * mm, "end": v(7.46, 6.84) * mm});
            skLineSegment(sketch, "E163.right", {"start": v(5.43, 8.1) * mm, "end": v(7.46, 8.1) * mm});
            skLineSegment(sketch, "E164.1.0", {"start": v(14.3, -2.03) * mm, "end": v(14.3, 0) * mm});
            skLineSegment(sketch, "E164.1.1", {"start": v(15.57, 0) * mm, "end": v(14.3, 0) * mm});
            skLineSegment(sketch, "E164.1.2", {"start": v(15.57, -2.03) * mm, "end": v(15.57, 0) * mm});
            skLineSegment(sketch, "E164.2.0", {"start": v(24.44, 6.84) * mm, "end": v(22.4, 6.84) * mm});
            skLineSegment(sketch, "E164.2.1", {"start": v(22.4, 8.1) * mm, "end": v(22.4, 6.84) * mm});
            skLineSegment(sketch, "E164.2.2", {"start": v(24.44, 8.1) * mm, "end": v(22.4, 8.1) * mm});
            skLineSegment(sketch, "E164.3.0", {"start": v(15.57, 16.98) * mm, "end": v(15.57, 14.94) * mm});
            skLineSegment(sketch, "E164.3.1", {"start": v(14.3, 14.94) * mm, "end": v(15.57, 14.94) * mm});
            skLineSegment(sketch, "E164.3.2", {"start": v(14.3, 16.98) * mm, "end": v(14.3, 14.94) * mm});
            skArc(sketch, "E165.trimOffspring", {"start": v(14.3, 16.98) * mm, "mid": v(8.2, 14.2) * mm, "end": v(5.43, 8.1) * mm});
            skArc(sketch, "E166.trimOffspring", {"start": v(15.57, -2.03) * mm, "mid": v(21.67, 0.74) * mm, "end": v(24.44, 6.84) * mm});
            skArc(sketch, "E167.trimOffspring", {"start": v(24.44, 8.1) * mm, "mid": v(21.67, 14.2) * mm, "end": v(15.57, 16.98) * mm});
            skArc(sketch, "E168", {"start": v(-24.44, 6.84) * mm, "mid": v(-21.67, 0.74) * mm, "end": v(-15.57, -2.03) * mm});
            skLineSegment(sketch, "E169.top", {"start": v(-22.4, 6.84) * mm, "end": v(-22.4, 8.1) * mm});
            skLineSegment(sketch, "E169.left", {"start": v(-24.44, 6.84) * mm, "end": v(-22.4, 6.84) * mm});
            skLineSegment(sketch, "E169.right", {"start": v(-24.44, 8.1) * mm, "end": v(-22.4, 8.1) * mm});
            skLineSegment(sketch, "E170.1.0", {"start": v(-15.57, -2.03) * mm, "end": v(-15.57, 0) * mm});
            skLineSegment(sketch, "E170.1.1", {"start": v(-14.3, 0) * mm, "end": v(-15.57, 0) * mm});
            skLineSegment(sketch, "E170.1.2", {"start": v(-14.3, -2.03) * mm, "end": v(-14.3, 0) * mm});
            skLineSegment(sketch, "E170.2.0", {"start": v(-5.43, 6.84) * mm, "end": v(-7.46, 6.84) * mm});
            skLineSegment(sketch, "E170.2.1", {"start": v(-7.46, 8.1) * mm, "end": v(-7.46, 6.84) * mm});
            skLineSegment(sketch, "E170.2.2", {"start": v(-5.43, 8.1) * mm, "end": v(-7.46, 8.1) * mm});
            skLineSegment(sketch, "E170.3.0", {"start": v(-14.3, 16.98) * mm, "end": v(-14.3, 14.94) * mm});
            skLineSegment(sketch, "E170.3.1", {"start": v(-15.57, 14.94) * mm, "end": v(-14.3, 14.94) * mm});
            skLineSegment(sketch, "E170.3.2", {"start": v(-15.57, 16.98) * mm, "end": v(-15.57, 14.94) * mm});
            skArc(sketch, "E171.trimOffspring", {"start": v(-15.57, 16.98) * mm, "mid": v(-21.67, 14.2) * mm, "end": v(-24.44, 8.1) * mm});
            skArc(sketch, "E172.trimOffspring", {"start": v(-14.3, -2.03) * mm, "mid": v(-8.2, 0.74) * mm, "end": v(-5.43, 6.84) * mm});
            skArc(sketch, "E173.trimOffspring", {"start": v(-5.43, 8.1) * mm, "mid": v(-8.2, 14.2) * mm, "end": v(-14.3, 16.98) * mm});
            skSolve(sketch);
        }
        {
            var Q0;
            Q0=qCreatedBy(id+"F9.planeOp",FACE);
            var sketch = newSketch(context, id + "F20", { "sketchPlane" : qUnion([Q0])});
            skArc(sketch, "E174", {"start": v(5.43, 6.84) * mm, "mid": v(8.2, 0.74) * mm, "end": v(14.3, -2.03) * mm});
            skLineSegment(sketch, "E175.top", {"start": v(7.46, 6.84) * mm, "end": v(7.46, 8.1) * mm});
            skLineSegment(sketch, "E175.left", {"start": v(5.43, 6.84) * mm, "end": v(7.46, 6.84) * mm});
            skLineSegment(sketch, "E175.right", {"start": v(5.43, 8.1) * mm, "end": v(7.46, 8.1) * mm});
            skLineSegment(sketch, "E176.1.0", {"start": v(14.3, -2.03) * mm, "end": v(14.3, 0) * mm});
            skLineSegment(sketch, "E176.1.1", {"start": v(15.57, 0) * mm, "end": v(14.3, 0) * mm});
            skLineSegment(sketch, "E176.1.2", {"start": v(15.57, -2.03) * mm, "end": v(15.57, 0) * mm});
            skLineSegment(sketch, "E176.2.0", {"start": v(24.44, 6.84) * mm, "end": v(22.4, 6.84) * mm});
            skLineSegment(sketch, "E176.2.1", {"start": v(22.4, 8.1) * mm, "end": v(22.4, 6.84) * mm});
            skLineSegment(sketch, "E176.2.2", {"start": v(24.44, 8.1) * mm, "end": v(22.4, 8.1) * mm});
            skLineSegment(sketch, "E176.3.0", {"start": v(15.57, 16.98) * mm, "end": v(15.57, 14.94) * mm});
            skLineSegment(sketch, "E176.3.1", {"start": v(14.3, 14.94) * mm, "end": v(15.57, 14.94) * mm});
            skLineSegment(sketch, "E176.3.2", {"start": v(14.3, 16.98) * mm, "end": v(14.3, 14.94) * mm});
            skArc(sketch, "E177.trimOffspring", {"start": v(14.3, 16.98) * mm, "mid": v(8.2, 14.2) * mm, "end": v(5.43, 8.1) * mm});
            skArc(sketch, "E178.trimOffspring", {"start": v(15.57, -2.03) * mm, "mid": v(21.67, 0.74) * mm, "end": v(24.44, 6.84) * mm});
            skArc(sketch, "E179.trimOffspring", {"start": v(24.44, 8.1) * mm, "mid": v(21.67, 14.2) * mm, "end": v(15.57, 16.98) * mm});
            skArc(sketch, "E180", {"start": v(-24.44, 6.84) * mm, "mid": v(-21.67, 0.74) * mm, "end": v(-15.57, -2.03) * mm});
            skLineSegment(sketch, "E181.top", {"start": v(-22.4, 6.84) * mm, "end": v(-22.4, 8.1) * mm});
            skLineSegment(sketch, "E181.left", {"start": v(-24.44, 6.84) * mm, "end": v(-22.4, 6.84) * mm});
            skLineSegment(sketch, "E181.right", {"start": v(-24.44, 8.1) * mm, "end": v(-22.4, 8.1) * mm});
            skLineSegment(sketch, "E182.1.0", {"start": v(-15.57, -2.03) * mm, "end": v(-15.57, 0) * mm});
            skLineSegment(sketch, "E182.1.1", {"start": v(-14.3, 0) * mm, "end": v(-15.57, 0) * mm});
            skLineSegment(sketch, "E182.1.2", {"start": v(-14.3, -2.03) * mm, "end": v(-14.3, 0) * mm});
            skLineSegment(sketch, "E182.2.0", {"start": v(-5.43, 6.84) * mm, "end": v(-7.46, 6.84) * mm});
            skLineSegment(sketch, "E182.2.1", {"start": v(-7.46, 8.1) * mm, "end": v(-7.46, 6.84) * mm});
            skLineSegment(sketch, "E182.2.2", {"start": v(-5.43, 8.1) * mm, "end": v(-7.46, 8.1) * mm});
            skLineSegment(sketch, "E182.3.0", {"start": v(-14.3, 16.98) * mm, "end": v(-14.3, 14.94) * mm});
            skLineSegment(sketch, "E182.3.1", {"start": v(-15.57, 14.94) * mm, "end": v(-14.3, 14.94) * mm});
            skLineSegment(sketch, "E182.3.2", {"start": v(-15.57, 16.98) * mm, "end": v(-15.57, 14.94) * mm});
            skArc(sketch, "E183.trimOffspring", {"start": v(-15.57, 16.98) * mm, "mid": v(-21.67, 14.2) * mm, "end": v(-24.44, 8.1) * mm});
            skArc(sketch, "E184.trimOffspring", {"start": v(-14.3, -2.03) * mm, "mid": v(-8.2, 0.74) * mm, "end": v(-5.43, 6.84) * mm});
            skArc(sketch, "E185.trimOffspring", {"start": v(-5.43, 8.1) * mm, "mid": v(-8.2, 14.2) * mm, "end": v(-14.3, 16.98) * mm});
            skSolve(sketch);
        }
        {
            var Q0;
            Q0 = qSketchRegion(id + "F0", true);
            extrude(context, id + "F21", {"entities" : qUnion([Q0]), "endBound" : BoundingType.SYMMETRIC, "depth" : 1.27 * mm, "offsetDistance" : 25.4 * mm});
        }
        {
            var Q0;
            Q0 = qSketchRegion(id + "F1", true);
            extrude(context, id + "F22", {"entities" : qUnion([Q0]), "operationType" : NewBodyOperationType.ADD, "endBound" : BoundingType.SYMMETRIC, "depth" : 1.27 * mm, "offsetDistance" : 25.4 * mm});
        }
        {
            var Q0;
            Q0 = qSketchRegion(id + "F14", true);
            extrude(context, id + "F23", {"entities" : qUnion([Q0]), "operationType" : NewBodyOperationType.ADD, "endBound" : BoundingType.SYMMETRIC, "depth" : 1.27 * mm, "offsetDistance" : 25.4 * mm});
        }
        {
            var Q0;
            Q0 = qSketchRegion(id + "F15", true);
            extrude(context, id + "F24", {"entities" : qUnion([Q0]), "endBound" : BoundingType.SYMMETRIC, "depth" : 1.27 * mm, "offsetDistance" : 25.4 * mm});
        }
        {
            var Q0;
            Q0 = qSketchRegion(id + "F17", true);
            extrude(context, id + "F25", {"entities" : qUnion([Q0]), "endBound" : BoundingType.SYMMETRIC, "depth" : 1.27 * mm, "offsetDistance" : 25.4 * mm});
        }
        {
            var Q0;
            Q0 = qSketchRegion(id + "F18", true);
            extrude(context, id + "F26", {"entities" : qUnion([Q0]), "endBound" : BoundingType.SYMMETRIC, "depth" : 1.27 * mm, "offsetDistance" : 25.4 * mm});
        }
        {
            var Q0;
            Q0 = qSketchRegion(id + "F19", true);
            extrude(context, id + "F27", {"entities" : qUnion([Q0]), "endBound" : BoundingType.SYMMETRIC, "depth" : 1.27 * mm, "offsetDistance" : 25.4 * mm});
        }
        {
            var Q0;
            Q0 = qSketchRegion(id + "F20", true);
            extrude(context, id + "F28", {"entities" : qUnion([Q0]), "endBound" : BoundingType.SYMMETRIC, "depth" : 1.27 * mm, "offsetDistance" : 25.4 * mm});
        }
        {
            var Q0;
            Q0=qCreatedBy(makeId("Front.planeOp"),FACE);
            var sketch = newSketch(context, id + "F29", { "sketchPlane" : qUnion([Q0])});
            skPoint(sketch, "E186.middle", {"position": v(0, 0) * mm});
            skCircle(sketch, "E187", {"center": v(19.05, 14.99) * mm, "radius": 9.53 * mm});
            skCircle(sketch, "E188", {"center": v(49.02, -14.99) * mm, "radius": 9.53 * mm});
            skCircle(sketch, "E189", {"center": v(163.32, -14.99) * mm, "radius": 9.53 * mm});
            skLineSegment(sketch, "E190", {"start": v(12.31, 8.25) * mm, "end": v(42.29, -21.72) * mm});
            skLineSegment(sketch, "E191", {"start": v(25.79, 21.72) * mm, "end": v(55.76, -8.25) * mm});
            skLineSegment(sketch, "E192", {"start": v(49.02, -24.51) * mm, "end": v(163.32, -24.51) * mm});
            skLineSegment(sketch, "E193", {"start": v(52.97, -5.46) * mm, "end": v(163.32, -5.46) * mm});
            skCircle(sketch, "E194", {"center": v(163.32, -14.99) * mm, "radius": 3.18 * mm});
            skCircle(sketch, "E195", {"center": v(19.05, 14.99) * mm, "radius": 1.56 * mm});
            skCircle(sketch, "E196", {"center": v(34.04, 0) * mm, "radius": 2.92 * mm});
            skLineSegment(sketch, "E197.0.0", {"start": v(-5.43, 8.1) * mm, "end": v(-5.43, 6.83) * mm});
            skLineSegment(sketch, "E197.0.1", {"start": v(-5.43, 6.83) * mm, "end": v(-9.5, 6.83) * mm});
            skArc(sketch, "E197.0.2", {"start": v(-9.5, 6.84) * mm, "mid": v(-6.74, 0.74) * mm, "end": v(-0.64, -2.03) * mm});
            skLineSegment(sketch, "E197.0.3", {"start": v(-0.64, -2.03) * mm, "end": v(-0.64, 2.03) * mm});
            skLineSegment(sketch, "E197.0.4", {"start": v(-0.64, 2.03) * mm, "end": v(0.64, 2.03) * mm});
            skLineSegment(sketch, "E197.0.5", {"start": v(0.63, 2.03) * mm, "end": v(0.63, -2.03) * mm});
            skArc(sketch, "E197.0.6", {"start": v(0.64, -2.03) * mm, "mid": v(6.74, 0.74) * mm, "end": v(9.5, 6.84) * mm});
            skLineSegment(sketch, "E197.0.7", {"start": v(9.5, 6.83) * mm, "end": v(5.43, 6.83) * mm});
            skLineSegment(sketch, "E197.0.8", {"start": v(5.43, 6.83) * mm, "end": v(5.43, 8.1) * mm});
            skLineSegment(sketch, "E197.0.9", {"start": v(9.5, 8.1) * mm, "end": v(5.43, 8.1) * mm});
            skArc(sketch, "E197.0.10", {"start": v(9.5, 8.1) * mm, "mid": v(6.74, 14.2) * mm, "end": v(0.63, 16.98) * mm});
            skLineSegment(sketch, "E197.0.11", {"start": v(0.64, 16.98) * mm, "end": v(0.64, 12.91) * mm});
            skLineSegment(sketch, "E197.0.12", {"start": v(0.64, 12.91) * mm, "end": v(-0.64, 12.91) * mm});
            skLineSegment(sketch, "E197.0.13", {"start": v(-0.64, 12.91) * mm, "end": v(-0.64, 16.98) * mm});
            skArc(sketch, "E197.0.14", {"start": v(-0.64, 16.98) * mm, "mid": v(-6.74, 14.2) * mm, "end": v(-9.5, 8.1) * mm});
            skLineSegment(sketch, "E197.0.15", {"start": v(-9.5, 8.1) * mm, "end": v(-5.43, 8.1) * mm});
            skCircle(sketch, "E198", {"center": v(0, 7.47) * mm, "radius": 9.53 * mm});
            skCircle(sketch, "E199.MirrorC", {"center": v(49.02, 14.99) * mm, "radius": 9.53 * mm});
            skLineSegment(sketch, "E200.MirrorCS", {"start": v(49.02, 24.51) * mm, "end": v(163.32, 24.51) * mm});
            skCircle(sketch, "E201.MirrorC", {"center": v(163.32, 14.99) * mm, "radius": 9.53 * mm});
            skCircle(sketch, "E202.MirrorC", {"center": v(19.05, -14.99) * mm, "radius": 9.53 * mm});
            skCircle(sketch, "E203.MirrorC", {"center": v(19.05, -14.99) * mm, "radius": 1.56 * mm});
            skLineSegment(sketch, "E204.MirrorCS", {"start": v(12.31, -8.25) * mm, "end": v(42.29, 21.72) * mm});
            skLineSegment(sketch, "E205.MirrorCS", {"start": v(25.79, -21.72) * mm, "end": v(55.76, 8.25) * mm});
            skLineSegment(sketch, "E206", {"start": v(49.02, 24.51) * mm, "end": v(-14.94, 24.51) * mm});
            skLineSegment(sketch, "E207", {"start": v(-14.94, 24.51) * mm, "end": v(-14.94, 7.47) * mm});
            skLineSegment(sketch, "E208", {"start": v(-14.94, 7.47) * mm, "end": v(-9.53, 7.47) * mm});
            skLineSegment(sketch, "E209", {"start": v(20.57, 0) * mm, "end": v(13.1, 7.47) * mm});
            skLineSegment(sketch, "E210", {"start": v(13.1, 7.47) * mm, "end": v(9.53, 7.47) * mm});
            skArc(sketch, "E211", {"start": v(34.04, 16.55) * mm, "mid": v(32.47, 14.99) * mm, "end": v(34.04, 13.42) * mm});
            skLineSegment(sketch, "E212", {"start": v(49.02, 16.55) * mm, "end": v(34.04, 16.55) * mm});
            skLineSegment(sketch, "E213", {"start": v(34.04, 13.42) * mm, "end": v(49.02, 13.42) * mm});
            skLineSegment(sketch, "E214", {"start": v(49.02, -24.51) * mm, "end": v(19.05, -24.51) * mm});
            skPoint(sketch, "E215.orphan", {"position": v(49.02, -5.46) * mm});
            skPoint(sketch, "E216.orphan", {"position": v(49.02, 5.46) * mm});
            skPoint(sketch, "E217.MirrorCS.end.orphan", {"position": v(163.32, 5.46) * mm});
            skLineSegment(sketch, "E218.MirrorCS", {"start": v(34.04, -13.42) * mm, "end": v(49.02, -13.42) * mm});
            skLineSegment(sketch, "E219.MirrorCS", {"start": v(49.02, -16.55) * mm, "end": v(34.04, -16.55) * mm});
            skArc(sketch, "E220.MirrorCS", {"start": v(34.04, -16.55) * mm, "mid": v(32.47, -14.99) * mm, "end": v(34.04, -13.42) * mm});
            skCircle(sketch, "E221.MirrorC", {"center": v(49.02, -14.99) * mm, "radius": 1.56 * mm});
            skCircle(sketch, "E222.MirrorC", {"center": v(49.02, 14.99) * mm, "radius": 1.56 * mm});
            skSolve(sketch);
        }
        {
            var Q0;
            {var subQ0=sQuery(id+"F29.wireOp",EDGE,"vylgdZOV-wlnO-5GiQ-4Z5u-kFAQEyezIKrT");var subQ3=sQuery(id+"F29.wireOp",EDGE,"E196");var subQ4=makeQuery(id+"F29.imprint","INTERSECT",VERTEX,{"disambiguationData":[OD(0.0)],"derivedFrom":[subQ3,subQ0]});Q0=makeQuery(id+"F29.imprint","IMPRINT",FACE,{"disambiguationData":[TD([[makeQuery(id+"F29.imprint","IMPRINT",EDGE,{"disambiguationData":[TD([[subQ4,1.0]])],"derivedFrom":subQ3}),-1.0]])]});}
            var Q1;
            {var subQ1=sQuery(id+"F29.wireOp",EDGE,"E191");var subQ5=sQuery(id+"F29.wireOp",EDGE,"E188");var subQ6=makeQuery(id+"F29.imprint","INTERSECT",VERTEX,{"derivedFrom":[subQ5,subQ1]});Q1=makeQuery(id+"F29.imprint","IMPRINT",FACE,{"disambiguationData":[TD([[makeQuery(id+"F29.imprint","IMPRINT",EDGE,{"disambiguationData":[TD([[subQ6,-1.0]])],"derivedFrom":subQ5}),-1.0]])]});}
            var Q2;
            {var subQ5=sQuery(id+"F29.wireOp",EDGE,"E214");Q2=makeQuery(id+"F29.imprint","IMPRINT",FACE,{"disambiguationData":[TD([[makeQuery(id+"F29.imprint","IMPRINT",EDGE,{"derivedFrom":subQ5}),-1.0]])]});}
            var Q3;
            {var subQ5=sQuery(id+"F29.wireOp",EDGE,"poaX1E9F-8vOh-Af5Y-RYos-nzvz6UXeckZc");Q3=makeQuery(id+"F29.imprint","IMPRINT",FACE,{"disambiguationData":[TD([[makeQuery(id+"F29.imprint","IMPRINT",EDGE,{"derivedFrom":subQ5}),-1.0]])]});}
            var Q4;
            {var subQ0=sQuery(id+"F29.wireOp",EDGE,"E204.MirrorCS");var subQ4=sQuery(id+"F29.wireOp",EDGE,"E202.MirrorC");var subQ5=makeQuery(id+"F29.imprint","INTERSECT",VERTEX,{"derivedFrom":[subQ4,subQ0]});Q4=makeQuery(id+"F29.imprint","IMPRINT",FACE,{"disambiguationData":[TD([[makeQuery(id+"F29.imprint","IMPRINT",EDGE,{"disambiguationData":[TD([[subQ5,-1.0]])],"derivedFrom":subQ4}),1.0]])]});}
            var Q5;
            Q5=makeQuery(id+"F29.imprint","IMPRINT",FACE,{"disambiguationData":[TD([[makeQuery(id+"F29.imprint","IMPRINT",EDGE,{"derivedFrom":sQuery(id+"F29.wireOp",EDGE,"E203.MirrorC")}),1.0]])]});
            var Q6;
            {var subQ0=sQuery(id+"F29.wireOp",EDGE,"XR3941Fq-qXpe-0tIT-5MLG-pofaRQihjKdr");Q6=makeQuery(id+"F29.imprint","IMPRINT",FACE,{"disambiguationData":[TD([[makeQuery(id+"F29.imprint","IMPRINT",EDGE,{"derivedFrom":subQ0}),-1.0]])]});}
            var Q7;
            {var subQ0=sQuery(id+"F29.wireOp",EDGE,"E190");var subQ1=sQuery(id+"F29.wireOp",EDGE,"E188");var subQ2=makeQuery(id+"F29.imprint","INTERSECT",VERTEX,{"derivedFrom":[subQ1,subQ0]});Q7=makeQuery(id+"F29.imprint","IMPRINT",FACE,{"disambiguationData":[TD([[makeQuery(id+"F29.imprint","IMPRINT",EDGE,{"disambiguationData":[TD([[subQ2,1.0]])],"derivedFrom":subQ1}),-1.0]])]});}
            extrude(context, id + "F30", {"entities" : qUnion([Q0, Q1, Q2, Q3, Q4, Q5, Q6, Q7]), "endBound" : BoundingType.SYMMETRIC, "depth" : 8.25 * mm, "offsetDistance" : 25.4 * mm});
        }
        {
            var Q0;
            {var subQ5=sQuery(id+"F29.wireOp",EDGE,"c6e4ec31-f847-44ba-bb0c-400d360d5408.0.8");Q0=makeQuery(id+"F29.imprint","IMPRINT",FACE,{"disambiguationData":[TD([[makeQuery(id+"F29.imprint","IMPRINT",EDGE,{"derivedFrom":subQ5}),1.0]])]});}
            var Q1;
            {var subQ0=sQuery(id+"F29.wireOp",EDGE,"c6e4ec31-f847-44ba-bb0c-400d360d5408.0.8");Q1=makeQuery(id+"F29.imprint","IMPRINT",FACE,{"disambiguationData":[TD([[makeQuery(id+"F29.imprint","IMPRINT",EDGE,{"derivedFrom":subQ0}),-1.0]])]});}
            var Q2;
            Q2=makeQuery(id+"F29.imprint","IMPRINT",FACE,{"disambiguationData":[TD([[makeQuery(id+"F29.imprint","IMPRINT",EDGE,{"derivedFrom":sQuery(id+"F29.wireOp",EDGE,"E195")}),-1.0]])]});
            var Q3;
            {var subQ0=sQuery(id+"F29.wireOp",EDGE,"E209");Q3=makeQuery(id+"F29.imprint","IMPRINT",FACE,{"disambiguationData":[TD([[makeQuery(id+"F29.imprint","IMPRINT",EDGE,{"derivedFrom":subQ0}),-1.0]])]});}
            var Q4;
            {var subQ0=sQuery(id+"F29.wireOp",EDGE,"vylgdZOV-wlnO-5GiQ-4Z5u-kFAQEyezIKrT");var subQ7=sQuery(id+"F29.wireOp",EDGE,"E196");var subQ8=makeQuery(id+"F29.imprint","INTERSECT",VERTEX,{"disambiguationData":[OD(0.0)],"derivedFrom":[subQ7,subQ0]});Q4=makeQuery(id+"F29.imprint","IMPRINT",FACE,{"disambiguationData":[TD([[makeQuery(id+"F29.imprint","IMPRINT",EDGE,{"disambiguationData":[TD([[subQ8,-1.0]])],"derivedFrom":subQ7}),-1.0]])]});}
            var Q5;
            {var subQ0=sQuery(id+"F29.wireOp",EDGE,"E205.MirrorCS");var subQ5=sQuery(id+"F29.wireOp",EDGE,"E199.MirrorC");var subQ6=makeQuery(id+"F29.imprint","INTERSECT",VERTEX,{"derivedFrom":[subQ5,subQ0]});Q5=makeQuery(id+"F29.imprint","IMPRINT",FACE,{"disambiguationData":[TD([[makeQuery(id+"F29.imprint","IMPRINT",EDGE,{"disambiguationData":[TD([[subQ6,-1.0]])],"derivedFrom":subQ5}),1.0]])]});}
            var Q6;
            {var subQ4=sQuery(id+"F29.wireOp",EDGE,"2baa67ee-4265-4809-a2a3-f695d8c220ac0.MirrorC");Q6=makeQuery(id+"F29.imprint","IMPRINT",FACE,{"disambiguationData":[TD([[makeQuery(id+"F29.imprint","IMPRINT",EDGE,{"derivedFrom":subQ4}),1.0]])]});}
            var Q7;
            {var subQ7=sQuery(id+"F29.wireOp",EDGE,"E191");var subQ8=sQuery(id+"F29.wireOp",EDGE,"E187");var subQ9=makeQuery(id+"F29.imprint","INTERSECT",VERTEX,{"derivedFrom":[subQ8,subQ7]});Q7=makeQuery(id+"F29.imprint","IMPRINT",FACE,{"disambiguationData":[TD([[makeQuery(id+"F29.imprint","IMPRINT",EDGE,{"disambiguationData":[TD([[subQ9,-1.0]])],"derivedFrom":subQ8}),-1.0]])]});}
            var Q8;
            {var subQ0=sQuery(id+"F29.wireOp",EDGE,"E204.MirrorCS");var subQ1=sQuery(id+"F29.wireOp",EDGE,"E199.MirrorC");var subQ2=makeQuery(id+"F29.imprint","INTERSECT",VERTEX,{"derivedFrom":[subQ1,subQ0]});Q8=makeQuery(id+"F29.imprint","IMPRINT",FACE,{"disambiguationData":[TD([[makeQuery(id+"F29.imprint","IMPRINT",EDGE,{"disambiguationData":[TD([[subQ2,1.0]])],"derivedFrom":subQ1}),1.0]])]});}
            extrude(context, id + "F31", {"entities" : qUnion([Q0, Q1, Q2, Q3, Q4, Q5, Q6, Q7, Q8]), "endBound" : BoundingType.SYMMETRIC, "depth" : 1.59 * mm, "offsetDistance" : 25.4 * mm});
        }
        {
            var Q0;
            Q0=qCreatedBy(makeId("Front.planeOp"),FACE);
            var sketch = newSketch(context, id + "F32", { "sketchPlane" : qUnion([Q0])});
            skArc(sketch, "E223.0.0", {"start": v(49.02, -24.51) * mm, "mid": v(57.82, -18.63) * mm, "end": v(55.76, -8.25) * mm});
            skLineSegment(sketch, "E224.0.2", {"start": v(19.05, -24.51) * mm, "end": v(49.02, -24.51) * mm});
            skArc(sketch, "E225.0.0", {"start": v(37.21, 0) * mm, "mid": v(34.04, -3.18) * mm, "end": v(30.86, 0) * mm});
            skLineSegment(sketch, "E225.0.1", {"start": v(30.86, 0) * mm, "end": v(20.57, 0) * mm});
            skLineSegment(sketch, "E225.0.6", {"start": v(47.5, 0) * mm, "end": v(37.21, 0) * mm});
            skLineSegment(sketch, "E226.0.0", {"start": v(3.96, -24.51) * mm, "end": v(19.05, -24.51) * mm});
            skLineSegment(sketch, "E226.0.3", {"start": v(13.07, -7.5) * mm, "end": v(3.96, -7.5) * mm});
            skLineSegment(sketch, "E226.0.4", {"start": v(3.96, -7.5) * mm, "end": v(3.96, -12.83) * mm});
            skLineSegment(sketch, "E226.0.5", {"start": v(3.96, -12.83) * mm, "end": v(0.85, -12.83) * mm});
            skLineSegment(sketch, "E226.0.6", {"start": v(0.85, -12.83) * mm, "end": v(0.85, -19.18) * mm});
            skLineSegment(sketch, "E226.0.7", {"start": v(0.85, -19.18) * mm, "end": v(3.96, -19.18) * mm});
            skLineSegment(sketch, "E226.0.8", {"start": v(3.96, -19.18) * mm, "end": v(3.96, -24.51) * mm});
            skCircle(sketch, "E227.0", {"center": v(19.05, -14.99) * mm, "radius": 1.56 * mm});
            skLineSegment(sketch, "E228.0", {"start": v(13.07, -7.5) * mm, "end": v(20.57, 0) * mm});
            skLineSegment(sketch, "E229.0", {"start": v(47.5, 0) * mm, "end": v(55.76, -8.25) * mm});
            skPoint(sketch, "E224.0.4.start.orphan", {"position": v(42.29, -21.72) * mm});
            skSolve(sketch);
        }
        {
            var Q0;
            Q0 = qSketchRegion(id + "F32", true);
            extrude(context, id + "F33", {"entities" : qUnion([Q0]), "endBound" : BoundingType.SYMMETRIC, "depth" : 7.94 * mm, "offsetDistance" : 25.4 * mm});
        }
        {
            var Q0;
            Q0=makeQuery(id+"F30.opExtrude","SWEPT_BODY",BODY,{"disambiguationData":[OSD([sQuery(id+"F29.wireOp",EDGE,"E188"),sQuery(id+"F29.wireOp",EDGE,"E191"),sQuery(id+"F29.wireOp",EDGE,"E205.MirrorCS"),sQuery(id+"F29.wireOp",EDGE,"E218.MirrorCS")])]});
            deleteBodies(context, id + "F34", {"entities" : qUnion([Q0])});
        }
        {
            var Q0;
            Q0=makeQuery(id+"F28.opExtrude","SWEPT_BODY",BODY,{"disambiguationData":[OSD([sQuery(id+"F20.wireOp",EDGE,"E180"),sQuery(id+"F20.wireOp",EDGE,"E181.top"),sQuery(id+"F20.wireOp",EDGE,"E181.left"),sQuery(id+"F20.wireOp",EDGE,"E181.right"),sQuery(id+"F20.wireOp",EDGE,"E182.1.0"),sQuery(id+"F20.wireOp",EDGE,"E182.1.1"),sQuery(id+"F20.wireOp",EDGE,"E182.1.2"),sQuery(id+"F20.wireOp",EDGE,"E182.2.0"),sQuery(id+"F20.wireOp",EDGE,"E182.2.1"),sQuery(id+"F20.wireOp",EDGE,"E182.2.2"),sQuery(id+"F20.wireOp",EDGE,"E182.3.0"),sQuery(id+"F20.wireOp",EDGE,"E182.3.1"),sQuery(id+"F20.wireOp",EDGE,"E182.3.2"),sQuery(id+"F20.wireOp",EDGE,"E183.trimOffspring"),sQuery(id+"F20.wireOp",EDGE,"E184.trimOffspring"),sQuery(id+"F20.wireOp",EDGE,"E185.trimOffspring")])]});
            deleteBodies(context, id + "F35", {"entities" : qUnion([Q0])});
        }
        {
            var Q0;
            Q0=makeQuery(id+"F28.opExtrude","SWEPT_BODY",BODY,{"disambiguationData":[OSD([sQuery(id+"F20.wireOp",EDGE,"E174"),sQuery(id+"F20.wireOp",EDGE,"E175.top"),sQuery(id+"F20.wireOp",EDGE,"E175.left"),sQuery(id+"F20.wireOp",EDGE,"E175.right"),sQuery(id+"F20.wireOp",EDGE,"E176.1.0"),sQuery(id+"F20.wireOp",EDGE,"E176.1.1"),sQuery(id+"F20.wireOp",EDGE,"E176.1.2"),sQuery(id+"F20.wireOp",EDGE,"E176.2.0"),sQuery(id+"F20.wireOp",EDGE,"E176.2.1"),sQuery(id+"F20.wireOp",EDGE,"E176.2.2"),sQuery(id+"F20.wireOp",EDGE,"E176.3.0"),sQuery(id+"F20.wireOp",EDGE,"E176.3.1"),sQuery(id+"F20.wireOp",EDGE,"E176.3.2"),sQuery(id+"F20.wireOp",EDGE,"E177.trimOffspring"),sQuery(id+"F20.wireOp",EDGE,"E178.trimOffspring"),sQuery(id+"F20.wireOp",EDGE,"E179.trimOffspring")])]});
            deleteBodies(context, id + "F36", {"entities" : qUnion([Q0])});
        }
        {
            var Q0;
            Q0=makeQuery(id+"F27.opExtrude","SWEPT_BODY",BODY,{"disambiguationData":[OSD([sQuery(id+"F19.wireOp",EDGE,"E168"),sQuery(id+"F19.wireOp",EDGE,"E169.top"),sQuery(id+"F19.wireOp",EDGE,"E169.left"),sQuery(id+"F19.wireOp",EDGE,"E169.right"),sQuery(id+"F19.wireOp",EDGE,"E170.1.0"),sQuery(id+"F19.wireOp",EDGE,"E170.1.1"),sQuery(id+"F19.wireOp",EDGE,"E170.1.2"),sQuery(id+"F19.wireOp",EDGE,"E170.2.0"),sQuery(id+"F19.wireOp",EDGE,"E170.2.1"),sQuery(id+"F19.wireOp",EDGE,"E170.2.2"),sQuery(id+"F19.wireOp",EDGE,"E170.3.0"),sQuery(id+"F19.wireOp",EDGE,"E170.3.1"),sQuery(id+"F19.wireOp",EDGE,"E170.3.2"),sQuery(id+"F19.wireOp",EDGE,"E171.trimOffspring"),sQuery(id+"F19.wireOp",EDGE,"E172.trimOffspring"),sQuery(id+"F19.wireOp",EDGE,"E173.trimOffspring")])]});
            deleteBodies(context, id + "F37", {"entities" : qUnion([Q0])});
        }
    });
